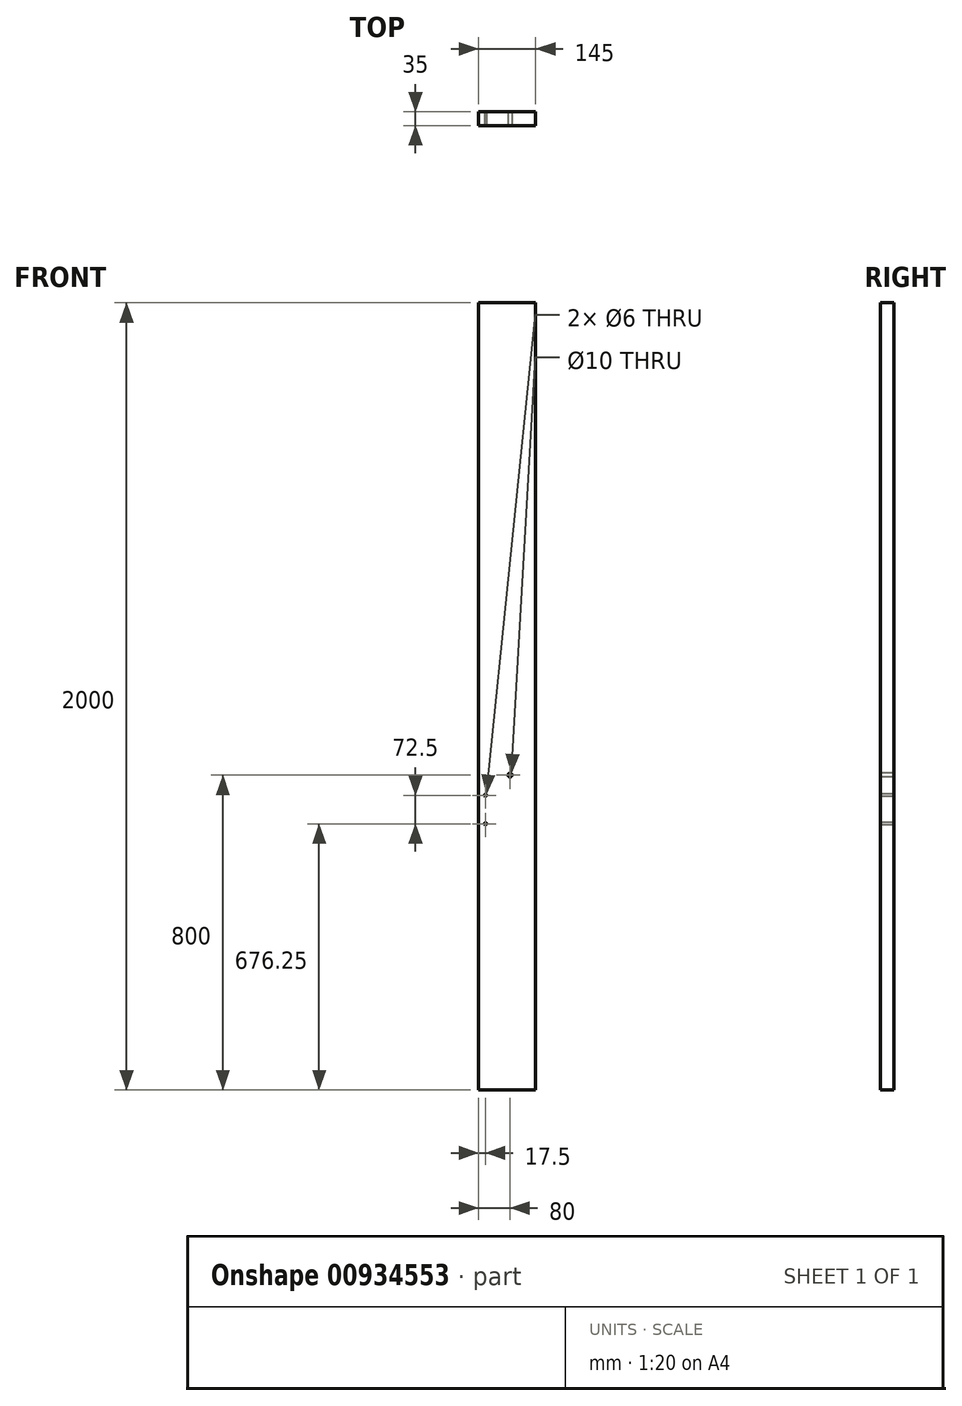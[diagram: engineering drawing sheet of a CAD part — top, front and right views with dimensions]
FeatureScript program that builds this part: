
annotation { "Feature Type Name" : "Feature", "Feature Type Description" : "" }
export const myFeature = defineFeature(function(context is Context, id is Id, definition is map)
    precondition{}
    {
        {
            var Q0;
            Q0=qCreatedBy(makeId("Front.planeOp"),FACE);
            var sketch = newSketch(context, id + "F0", { "sketchPlane" : qUnion([Q0])});
            skLineSegment(sketch, "E0.bottom", {"start": v(0, 0) * mm, "end": v(145, 0) * mm});
            skLineSegment(sketch, "E0.top", {"start": v(0, 2000) * mm, "end": v(145, 2000) * mm});
            skLineSegment(sketch, "E0.left", {"start": v(0, 0) * mm, "end": v(0, 2000) * mm});
            skLineSegment(sketch, "E0.right", {"start": v(145, 0) * mm, "end": v(145, 2000) * mm});
            skSolve(sketch);
        }
        {
            var Q0;
            Q0=makeQuery(id+"F0.imprint","IMPRINT",FACE,{"disambiguationData":[TD([[makeQuery(id+"F0.imprint","IMPRINT",EDGE,{"derivedFrom":sQuery(id+"F0.wireOp",EDGE,"E0.bottom")}),1.0]])]});
            extrude(context, id + "F1", {"entities" : qUnion([Q0]), "oppositeDirection" : true, "depth" : 35 * mm, "offsetDistance" : 25 * mm});
        }
        {
            var Q0;
            Q0=makeQuery(id+"F1.opExtrude","CAP_FACE",FACE,{"disambiguationData":[OSD([sQuery(id+"F0.wireOp",EDGE,"E0.bottom"),sQuery(id+"F0.wireOp",EDGE,"E0.top"),sQuery(id+"F0.wireOp",EDGE,"E0.left"),sQuery(id+"F0.wireOp",EDGE,"E0.right")])],"isStart":true});
            var sketch = newSketch(context, id + "F2", { "sketchPlane" : qUnion([Q0])});
            skCircle(sketch, "E1", {"center": v(80, 800) * mm, "radius": 5 * mm});
            skSolve(sketch);
        }
        {
            var Q0;
            Q0=makeQuery(id+"F2.imprint","IMPRINT",FACE,{"disambiguationData":[TD([[makeQuery(id+"F2.imprint","IMPRINT",EDGE,{"derivedFrom":sQuery(id+"F2.wireOp",EDGE,"E1")}),1.0]])]});
            extrude(context, id + "F3", {"entities" : qUnion([Q0]), "operationType" : NewBodyOperationType.REMOVE, "endBound" : BoundingType.THROUGH_ALL, "oppositeDirection" : true, "depth" : 25 * mm, "offsetDistance" : 25 * mm});
        }
        {
            var Q0;
            Q0=makeQuery(id+"F1.opExtrude","CAP_FACE",FACE,{"disambiguationData":[OSD([sQuery(id+"F0.wireOp",EDGE,"E0.bottom"),sQuery(id+"F0.wireOp",EDGE,"E0.top"),sQuery(id+"F0.wireOp",EDGE,"E0.left"),sQuery(id+"F0.wireOp",EDGE,"E0.right")])],"isStart":true});
            var sketch = newSketch(context, id + "F4", { "sketchPlane" : qUnion([Q0])});
            skLineSegment(sketch, "E2.bottom", {"start": v(0, 785) * mm, "end": v(35, 785) * mm, "construction": true});
            skLineSegment(sketch, "E2.top", {"start": v(0, 640) * mm, "end": v(35, 640) * mm, "construction": true});
            skLineSegment(sketch, "E2.left", {"start": v(0, 785) * mm, "end": v(0, 640) * mm, "construction": true});
            skLineSegment(sketch, "E2.right", {"start": v(35, 785) * mm, "end": v(35, 640) * mm, "construction": true});
            skLineSegment(sketch, "E3", {"start": v(35, 785) * mm, "end": v(80, 785) * mm, "construction": true});
            skLineSegment(sketch, "E4", {"start": v(80, 785) * mm, "end": v(80, 800) * mm, "construction": true});
            skLineSegment(sketch, "E5", {"start": v(0, 712.5) * mm, "end": v(35, 712.5) * mm, "construction": true});
            skCircle(sketch, "E6", {"center": v(17.5, 676.25) * mm, "radius": 3 * mm});
            skCircle(sketch, "E7.MirrorC", {"center": v(17.5, 748.75) * mm, "radius": 3 * mm});
            skLineSegment(sketch, "E8", {"start": v(17.5, 712.5) * mm, "end": v(17.5, 640) * mm, "construction": true});
            skSolve(sketch);
        }
        {
            var Q0;
            Q0 = qSketchRegion(id + "F4", true);
            extrude(context, id + "F5", {"entities" : qUnion([Q0]), "operationType" : NewBodyOperationType.REMOVE, "endBound" : BoundingType.THROUGH_ALL, "oppositeDirection" : true, "depth" : 25 * mm, "offsetDistance" : 25 * mm});
        }
    });
